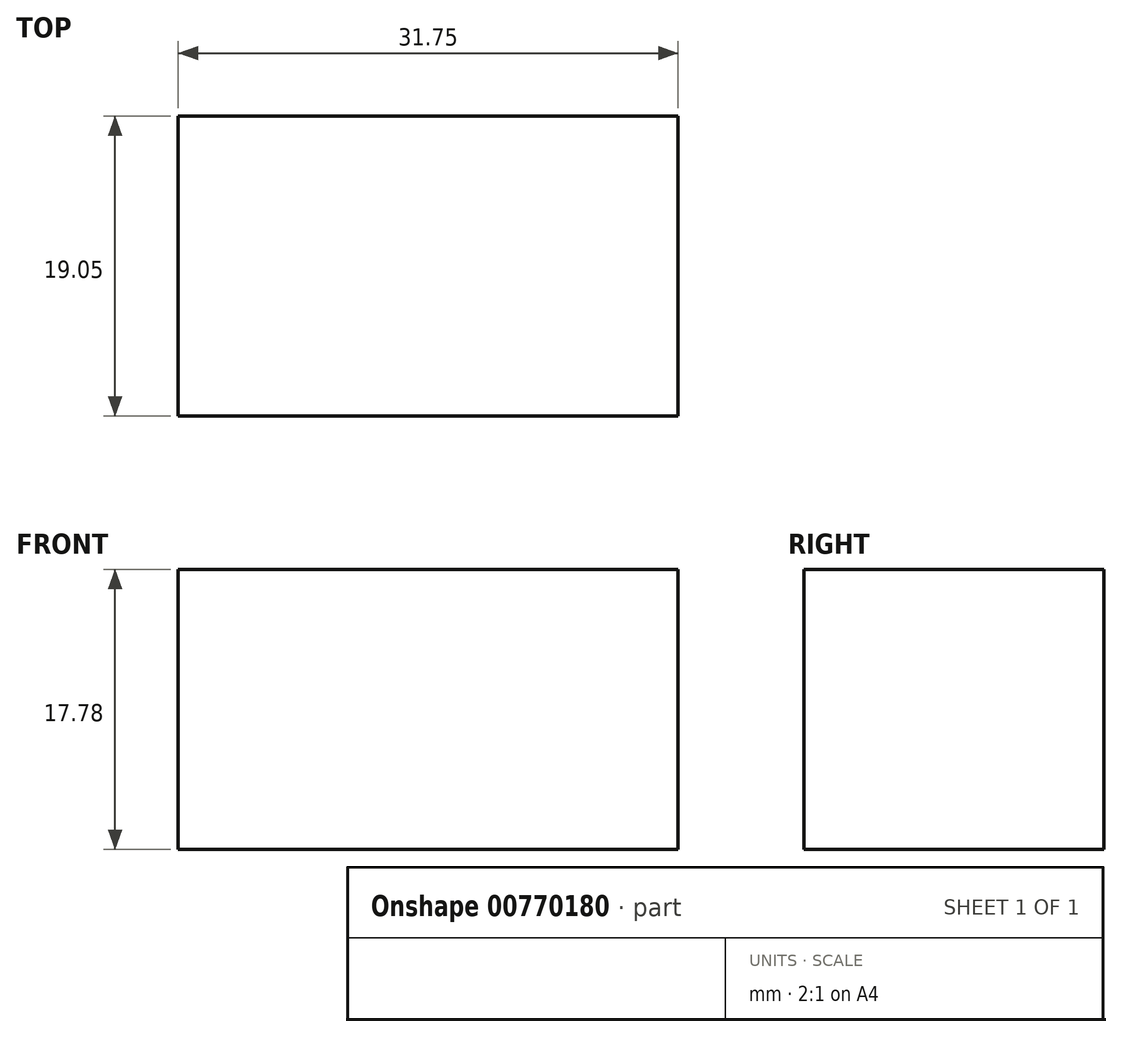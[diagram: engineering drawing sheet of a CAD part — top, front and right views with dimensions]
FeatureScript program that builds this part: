
annotation { "Feature Type Name" : "Feature", "Feature Type Description" : "" }
export const myFeature = defineFeature(function(context is Context, id is Id, definition is map)
    precondition{}
    {
        {
            var Q0;
            Q0=qCreatedBy(makeId("Right.planeOp"),FACE);
            var sketch = newSketch(context, id + "F0", { "sketchPlane" : qUnion([Q0])});
            skLineSegment(sketch, "E0.bottom", {"start": v(-19.05, 18.43) * mm, "end": v(0, 18.43) * mm});
            skLineSegment(sketch, "E0.top", {"start": v(-19.05, 36.21) * mm, "end": v(0, 36.21) * mm});
            skLineSegment(sketch, "E0.left", {"start": v(-19.05, 18.43) * mm, "end": v(-19.05, 36.21) * mm});
            skLineSegment(sketch, "E0.right", {"start": v(0, 18.43) * mm, "end": v(0, 36.21) * mm});
            skSolve(sketch);
        }
        {
            var Q0;
            Q0=makeQuery(id+"F0.imprint","IMPRINT",FACE,{"disambiguationData":[TD([[makeQuery(id+"F0.imprint","IMPRINT",EDGE,{"derivedFrom":sQuery(id+"F0.wireOp",EDGE,"E0.bottom")}),1.0]])]});
            extrude(context, id + "F1", {"entities" : qUnion([Q0]), "depth" : 31.75 * mm, "offsetDistance" : 25.4 * mm});
        }
    });
